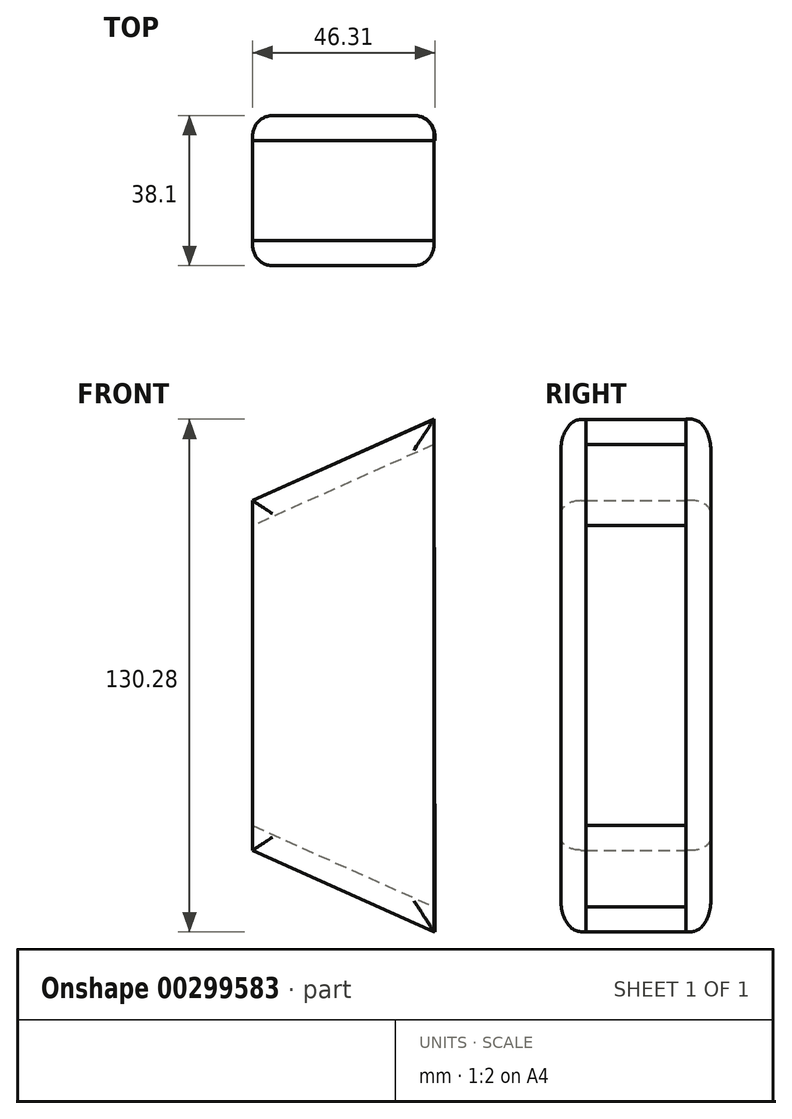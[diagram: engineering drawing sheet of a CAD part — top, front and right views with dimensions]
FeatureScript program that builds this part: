
annotation { "Feature Type Name" : "Feature", "Feature Type Description" : "" }
export const myFeature = defineFeature(function(context is Context, id is Id, definition is map)
    precondition{}
    {
        {
            var Q0;
            Q0=qCreatedBy(makeId("Front.planeOp"),FACE);
            var sketch = newSketch(context, id + "F0", { "sketchPlane" : qUnion([Q0])});
            skLineSegment(sketch, "E0", {"start": v(0, 0) * mm, "end": v(0, 76.2) * mm});
            skLineSegment(sketch, "E1", {"start": v(46.04, 0) * mm, "end": v(46.04, -20.64) * mm});
            skLineSegment(sketch, "E2", {"start": v(0, 0) * mm, "end": v(46.04, -20.64) * mm});
            skLineSegment(sketch, "E3", {"start": v(46.04, 76.2) * mm, "end": v(46.04, 0) * mm});
            skLineSegment(sketch, "E4", {"start": v(46.04, 76.2) * mm, "end": v(46.04, 96.84) * mm});
            skLineSegment(sketch, "E5", {"start": v(46.04, 96.84) * mm, "end": v(0, 76.2) * mm});
            skLineSegment(sketch, "E6", {"start": v(0, 0) * mm, "end": v(0, -6.35) * mm});
            skLineSegment(sketch, "E7", {"start": v(46.04, -20.64) * mm, "end": v(46.04, -26.99) * mm});
            skLineSegment(sketch, "E8", {"start": v(0, 76.2) * mm, "end": v(0, 82.55) * mm});
            skLineSegment(sketch, "E9", {"start": v(46.04, 96.84) * mm, "end": v(46.04, 103.19) * mm});
            skLineSegment(sketch, "E10", {"start": v(0, 82.55) * mm, "end": v(46.04, 103.19) * mm});
            skLineSegment(sketch, "E11", {"start": v(0, -6.35) * mm, "end": v(46.04, -26.99) * mm});
            skSolve(sketch);
        }
        {
            var Q0;
            Q0=makeQuery(id+"F0.imprint","IMPRINT",FACE,{"disambiguationData":[TD([[makeQuery(id+"F0.imprint","IMPRINT",EDGE,{"derivedFrom":sQuery(id+"F0.wireOp",EDGE,"E5")}),-1.0]])]});
            extrude(context, id + "F1", {"entities" : qUnion([Q0]), "depth" : 25.4 * mm});
        }
        {
            var Q0;
            Q0=makeQuery(id+"F0.imprint","IMPRINT",FACE,{"disambiguationData":[TD([[makeQuery(id+"F0.imprint","IMPRINT",EDGE,{"derivedFrom":sQuery(id+"F0.wireOp",EDGE,"E2")}),-1.0]])]});
            extrude(context, id + "F2", {"entities" : qUnion([Q0]), "depth" : 25.4 * mm});
        }
        {
            var Q0;
            Q0=qCreatedBy(makeId("Front.planeOp"),FACE);
            var sketch = newSketch(context, id + "F3", { "sketchPlane" : qUnion([Q0])});
            skLineSegment(sketch, "E12", {"start": v(46.13, 103.29) * mm, "end": v(0, 82.64) * mm});
            skLineSegment(sketch, "E13", {"start": v(0, 82.64) * mm, "end": v(0, -6.33) * mm});
            skLineSegment(sketch, "E14", {"start": v(0, -6.33) * mm, "end": v(46.31, -26.97) * mm});
            skLineSegment(sketch, "E15", {"start": v(46.31, -26.97) * mm, "end": v(46.13, 103.29) * mm});
            skSolve(sketch);
        }
        {
            var Q0;
            Q0 = qSketchRegion(id + "F3", true);
            extrude(context, id + "F4", {"entities" : qUnion([Q0]), "oppositeDirection" : true, "depth" : 6.35 * mm});
        }
        {
            var Q0;
            Q0=makeQuery(id+"F1.opExtrude","CAP_FACE",FACE,{"disambiguationData":[OSD([sQuery(id+"F0.wireOp",EDGE,"E5"),sQuery(id+"F0.wireOp",EDGE,"E8"),sQuery(id+"F0.wireOp",EDGE,"E9"),sQuery(id+"F0.wireOp",EDGE,"E10")])],"isStart":false});
            var sketch = newSketch(context, id + "F5", { "sketchPlane" : qUnion([Q0])});
            skLineSegment(sketch, "E16", {"start": v(0, 82.55) * mm, "end": v(46.04, 103.19) * mm});
            skLineSegment(sketch, "E17", {"start": v(46.04, 103.19) * mm, "end": v(46.04, -26.93) * mm});
            skLineSegment(sketch, "E18", {"start": v(46.04, -26.93) * mm, "end": v(0, -6.23) * mm});
            skLineSegment(sketch, "E19", {"start": v(0, -6.23) * mm, "end": v(0, 82.55) * mm});
            skSolve(sketch);
        }
        {
            var Q0;
            Q0 = qSketchRegion(id + "F5", true);
            extrude(context, id + "F6", {"entities" : qUnion([Q0]), "depth" : 6.35 * mm});
        }
        {
            var Q0;
            Q0=makeQuery(id+"F6.opExtrude","CAP_EDGE",EDGE,{"disambiguationData":[OSD([sQuery(id+"F5.wireOp",EDGE,"E18")])],"isStart":false});
            var Q1;
            Q1=makeQuery(id+"F6.opExtrude","CAP_FACE",FACE,{"disambiguationData":[OSD([sQuery(id+"F5.wireOp",EDGE,"E16"),sQuery(id+"F5.wireOp",EDGE,"E17"),sQuery(id+"F5.wireOp",EDGE,"E18"),sQuery(id+"F5.wireOp",EDGE,"E19")])],"isStart":false});
            fillet(context, id + "F7", {"entities" : qUnion([Q0, Q1]), "radius" : 5.08 * mm, "tangentPropagation" : true, "allowEdgeOverflow" : false});
        }
        {
            var Q0;
            Q0=makeQuery(id+"F4.opExtrude","CAP_EDGE",EDGE,{"disambiguationData":[OSD([sQuery(id+"F3.wireOp",EDGE,"E12")])],"isStart":false});
            var Q1;
            Q1=makeQuery(id+"F4.opExtrude","CAP_FACE",FACE,{"disambiguationData":[OSD([sQuery(id+"F3.wireOp",EDGE,"E12"),sQuery(id+"F3.wireOp",EDGE,"E13"),sQuery(id+"F3.wireOp",EDGE,"E14"),sQuery(id+"F3.wireOp",EDGE,"E15")])],"isStart":false});
            fillet(context, id + "F8", {"entities" : qUnion([Q0, Q1]), "radius" : 5.08 * mm, "tangentPropagation" : true, "allowEdgeOverflow" : false});
        }
    });
